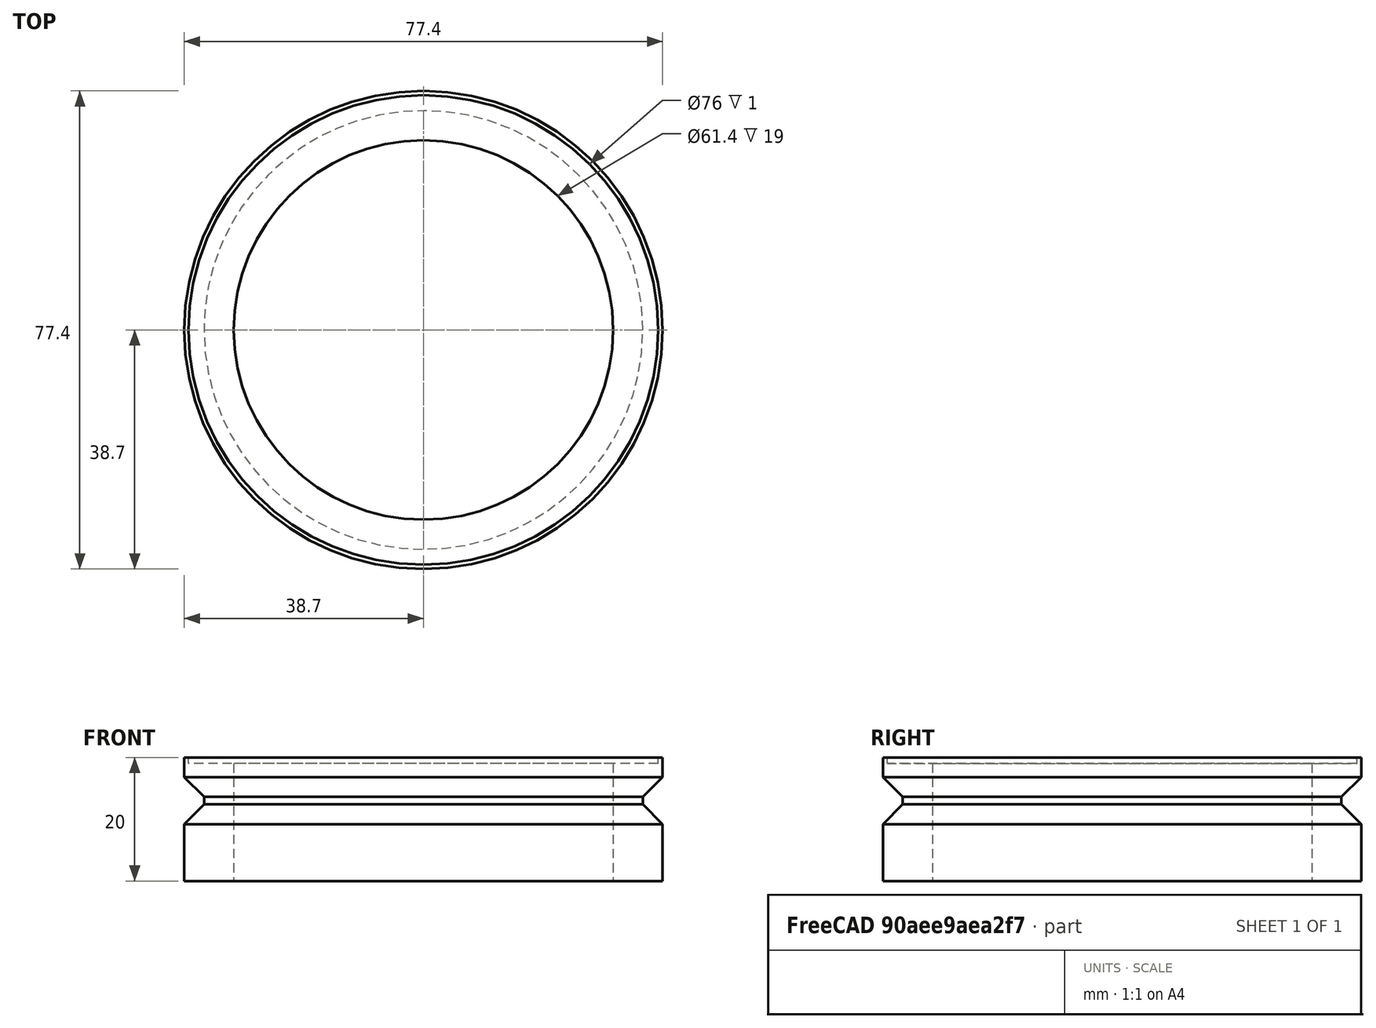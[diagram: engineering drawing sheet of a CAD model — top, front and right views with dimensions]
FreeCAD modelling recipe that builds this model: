
FCSTD DOCUMENT  (FreeCAD 0.16R6705 (Git))
Label: TestRace
License: All rights reserved
LicenseURL: http://en.wikipedia.org/wiki/All_rights_reserved
objects: Sketcher::SketchObject×1, PartDesign::Revolution×1
note: 3 computed .brp shape members not serialized (recipe doc carries the construction recipe); baked Part::Feature solids carry a one-line shape summary decoded from their .brp

FEATURE [Sketcher::SketchObject] Sketch019
  Placement = pos=(0,0,0) rot=(1,0,0;1.5708rad)
  sketch-geometry (14):
    g0: LineSegment StartX=38 StartY=20 StartZ=0 EndX=38.7 EndY=20 EndZ=0
    g1: LineSegment StartX=30.7 StartY=19 StartZ=0 EndX=38 EndY=19 EndZ=0
    g2: LineSegment StartX=38 StartY=19 StartZ=0 EndX=38 EndY=20 EndZ=0
    g3: LineSegment StartX=38.7 StartY=20 StartZ=0 EndX=38.7 EndY=16.8012 EndZ=0
    g4: LineSegment StartX=35.5 StartY=12.3988 StartZ=0 EndX=38.7 EndY=9.19878 EndZ=0
    g5: LineSegment StartX=38.7 StartY=9.19878 StartZ=0 EndX=38.7 EndY=0 EndZ=0
    g6: LineSegment [constr] StartX=38.7 StartY=16.8012 StartZ=0 EndX=38.7 EndY=9.19878 EndZ=0
    g7: LineSegment [constr] StartX=35.5 StartY=13 StartZ=0 EndX=39 EndY=13 EndZ=0
    g8: Circle [constr] CenterX=39 CenterY=13 CenterZ=0 NormalX=0 NormalY=0 NormalZ=1 Radius=2.9
    g9: LineSegment StartX=38.7 StartY=16.8012 StartZ=0 EndX=35.5 EndY=13.6012 EndZ=0
    g10: LineSegment StartX=35.5 StartY=13.6012 StartZ=0 EndX=35.5 EndY=12.3988 EndZ=0
    g11: GeomPoint [constr] X=36.1 Y=13 Z=0
    g12: LineSegment StartX=30.7 StartY=19 StartZ=0 EndX=30.7 EndY=0 EndZ=0
    g13: LineSegment StartX=30.7 StartY=0 StartZ=0 EndX=38.7 EndY=0 EndZ=0
  constraints (42):
    c: Horizontal(g0)
    c: Horizontal(g1)
    c: Coincident(g2,g0)
    c: Vertical(g2)
    c: Coincident(g2,g1)
    c: DistanceY(g1,g0) = 1
    c: DistanceX(g0,g0) = 0.7
    c: DistanceX(g-1,g5) = 38.7
    c: DistanceX(g-1,g1) = 38
    c: Coincident(g0,g3)
    c: Vertical(g3)
    c: Coincident(g4,g5)
    c: Vertical(g5)
    c: Vertical(g6)
    c: Coincident(g6,g3)
    c: Coincident(g4,g6)
    c: Horizontal(g7)
    c: PointOnObject(g8,g7)
    c: Coincident(g3,g9)
    c: Coincident(g9,g10)
    c: Coincident(g10,g4)
    c: Vertical(g10)
    c: Angle(g4,g9) = 1.5708
    c: Symmetric(g9,g4,g7)
    c: Tangent(g4,g8)
    c: Tangent(g9,g8)
    c: DistanceX(g4,g8) = 0.3
    c: Radius(g8) = 2.9
    c: PointOnObject(g11,g8)
    c: PointOnObject(g11,g7)
    c: DistanceX(g4,g11) = 0.6
    c: DistanceX(g-1,g8) = 39
    c: DistanceY(g8,g0) = 7
    c: Coincident(g8,g7)
    c: Coincident(g12,g1)
    c: PointOnObject(g12,g-1)
    c: Vertical(g12)
    c: Coincident(g13,g12)
    c: Coincident(g13,g5)
    c: Horizontal(g13)
    c: DistanceX(g12,g5) = 8
    c: DistanceY(g5,g0) = 20
FEATURE [PartDesign::Revolution] Revolution
  Angle = 360
  Axis = (0,0,1)
  Base = (0,0,0)
  Placement = pos=(0,0,0) rot=(1,0,0;1.5708rad)
  ReferenceAxis = -> Sketch019 [V_Axis]
  Reversed = true
  Sketch = -> Sketch019
